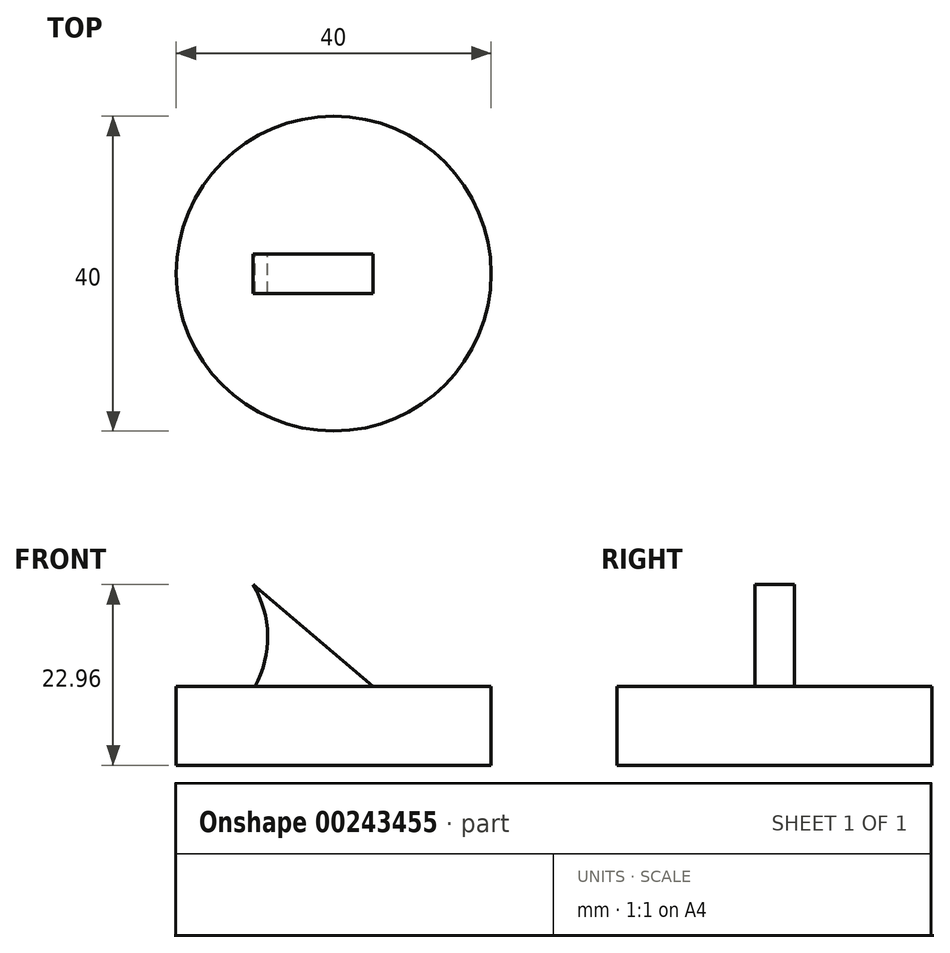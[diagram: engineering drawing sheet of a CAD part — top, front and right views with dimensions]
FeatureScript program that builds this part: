
annotation { "Feature Type Name" : "Feature", "Feature Type Description" : "" }
export const myFeature = defineFeature(function(context is Context, id is Id, definition is map)
    precondition{}
    {
        {
            var Q0;
            Q0=qCreatedBy(makeId("Top.planeOp"),FACE);
            var sketch = newSketch(context, id + "F0", { "sketchPlane" : qUnion([Q0])});
            skCircle(sketch, "E0", {"center": v(0, 0) * mm, "radius": 20 * mm});
            skSolve(sketch);
        }
        {
            var Q0;
            Q0=makeQuery(id+"F0.imprint","IMPRINT",FACE,{"disambiguationData":[TD([[makeQuery(id+"F0.imprint","IMPRINT",EDGE,{"derivedFrom":sQuery(id+"F0.wireOp",EDGE,"E0")}),1.0]])]});
            extrude(context, id + "F1", {"entities" : qUnion([Q0]), "depth" : 10 * mm});
        }
        {
            var Q0;
            Q0=makeQuery(id+"F1.opExtrude","CAP_FACE",FACE,{"disambiguationData":[OSD([sQuery(id+"F0.wireOp",EDGE,"E0")])],"isStart":false});
            cPlane(context, id + "F2", {"entities" : qUnion([Q0]), "cplaneType" : CPlaneType.OFFSET, "offset" : 0 * mm, "width" : 150 * mm, "height" : 150 * mm});
        }
        {
            var Q0;
            Q0=qCreatedBy(makeId("Front.planeOp"),FACE);
            var sketch = newSketch(context, id + "F3", { "sketchPlane" : qUnion([Q0])});
            skLineSegment(sketch, "E1", {"start": v(5, 10) * mm, "end": v(-10, 10) * mm});
            skLineSegment(sketch, "E2", {"start": v(5, 10) * mm, "end": v(-10.24, 22.96) * mm});
            skArc(sketch, "E3", {"start": v(-10, 10) * mm, "mid": v(-8.39, 16.51) * mm, "end": v(-10.24, 22.96) * mm});
            skSolve(sketch);
        }
        {
            var Q0;
            Q0 = qSketchRegion(id + "F3", true);
            extrude(context, id + "F4", {"entities" : qUnion([Q0]), "endBound" : BoundingType.SYMMETRIC, "depth" : 5 * mm});
        }
    });
